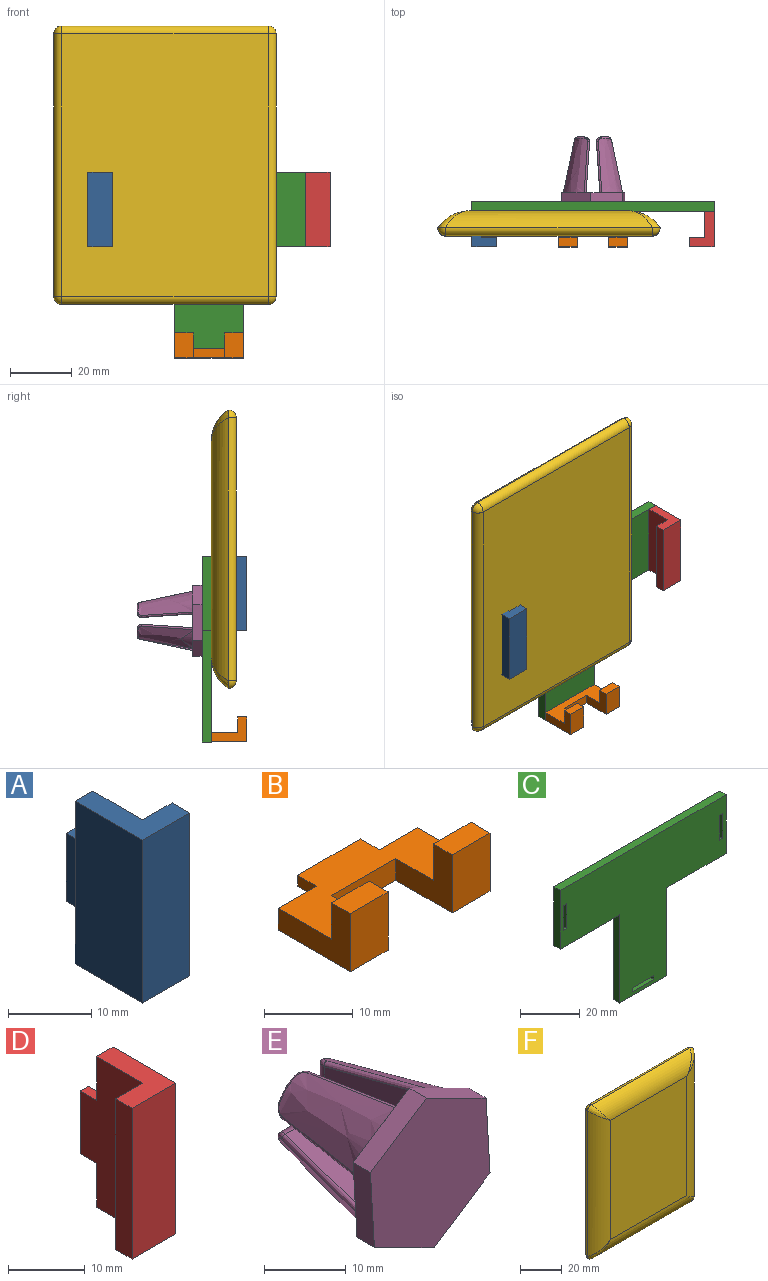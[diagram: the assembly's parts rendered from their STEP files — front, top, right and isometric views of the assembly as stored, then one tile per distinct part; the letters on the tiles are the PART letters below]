
ASSEMBLY  parts=6 mates=5
PART A: 12 faces, bbox 8x14.5x24 mm
  f0: plane 11.5x8mm, normal (0,0,-1), area 49.5mm2, adj f1,f4,f5,f6,f7,f11
  f1: plane 24x11.5mm, normal (1,0,0), area 234mm2, adj f0,f2,f3,f7,f8,f10,f11
  f2: plane 11.5x8mm, normal (0,0,1), area 49.5mm2, adj f1,f4,f5,f6,f7,f11
  f3: plane 10x1.5mm, normal (0,1,0), area 15mm2, adj f1,f8,f9,f10
  f4: plane 24x11.5mm, normal (-1,0,0), area 276mm2, adj f0,f2,f6,f11
  f5: plane 24x3mm, normal (1,0,0), area 72mm2, adj f0,f2,f6,f7
  f6: plane 24x8mm, normal (0,-1,0), area 192mm2, adj f0,f2,f4,f5
  f7: plane 24x5mm, normal (0,1,0), area 120mm2, adj f0,f1,f2,f5
  f8: plane 3x1.5mm, normal (0,0,1), area 4.5mm2, adj f1,f3,f9,f11
  f9: plane 10x3mm, normal (-1,0,0), area 30mm2, adj f3,f8,f10,f11
  f10: plane 3x1.5mm, normal (0,0,-1), area 4.5mm2, adj f1,f3,f9,f11
  f11: plane 24x3mm, normal (0,1,0), area 57mm2, adj f0,f1,f2,f4,f8,f9,f10
PART B: 18 faces, bbox 22.2x14.5x8 mm
  f0: plane 10x1.5mm, normal (0,1,0), area 15mm2, adj f1,f2,f3,f4
  f1: plane 22.2x11.5mm, normal (0,0,1), area 157.5mm2, adj f0,f3,f4,f5,f6,f7,f9,f12
  f2: plane 10x3mm, normal (0,0,-1), area 30mm2, adj f0,f3,f4,f5
  f3: plane 3x1.5mm, normal (-1,0,0), area 4.5mm2, adj f0,f1,f2,f5
  f4: plane 3x1.5mm, normal (1,0,0), area 4.5mm2, adj f0,f1,f2,f5
  f5: plane 22.2x3mm, normal (0,1,0), area 51.6mm2, adj f1,f2,f3,f4,f7,f8,f16
  f6: plane 9x8mm, normal (1,0,0), area 42mm2, adj f1,f8,f9,f10,f11,f17
  f7: plane 11.5x8mm, normal (-1,0,0), area 49.5mm2, adj f1,f5,f8,f9,f10,f11
  f8: plane 22.2x11.5mm, normal (0,0,-1), area 163.5mm2, adj f5,f6,f7,f11,f12,f15,f16,f17
  f9: plane 6x5mm, normal (0,1,0), area 30mm2, adj f1,f6,f7,f10
  f10: plane 6x3mm, normal (0,0,1), area 18mm2, adj f6,f7,f9,f11
  f11: plane 8x6mm, normal (0,-1,0), area 48mm2, adj f6,f7,f8,f10
  f12: plane 9x8mm, normal (-1,0,0), area 42mm2, adj f1,f8,f13,f14,f15,f17
  f13: plane 6x5mm, normal (0,1,0), area 30mm2, adj f1,f12,f14,f16
  f14: plane 6x3mm, normal (0,0,1), area 18mm2, adj f12,f13,f15,f16
  f15: plane 8x6mm, normal (0,-1,0), area 48mm2, adj f8,f12,f14,f16
  f16: plane 11.5x8mm, normal (1,0,0), area 49.5mm2, adj f1,f5,f8,f13,f14,f15
  f17: plane 10.2x3mm, normal (0,-1,0), area 30.6mm2, adj f1,f6,f8,f12
PART C: 22 faces, bbox 78.3x3x60 mm
  f0: plane 36x3mm, normal (-1,0,0), area 108mm2, adj f2,f3,f4,f5
  f1: plane 36x3mm, normal (1,0,0), area 108mm2, adj f2,f3,f4,f9
  f2: plane 22.2x3mm, normal (0,0,-1), area 66.6mm2, adj f0,f1,f3,f4
  f3: plane 78.3x60mm, normal (0,1,0), area 2629.9mm2, adj f0,f1,f2,f5,f6,f7,f8,f9
  f4: plane 78.3x60mm, normal (0,-1,0), area 2629.9mm2, adj f0,f1,f2,f5,f6,f7,f8,f9
  f5: plane 28.05x3mm, normal (0,0,-1), area 84.1mm2, adj f0,f3,f4,f8
  f6: plane 24x3mm, normal (1,0,0), area 72mm2, adj f3,f4,f7,f9
  f7: plane 78.3x3mm, normal (0,0,1), area 234.9mm2, adj f3,f4,f6,f8
  f8: plane 24x3mm, normal (-1,0,0), area 72mm2, adj f3,f4,f5,f7
  f9: plane 28.05x3mm, normal (0,0,-1), area 84.1mm2, adj f1,f3,f4,f6
  f10: plane 10.1x3mm, normal (1,0,0), area 30.3mm2, adj f3,f4,f11,f12
  f11: plane 3x1.6mm, normal (0,0,-1), area 4.8mm2, adj f3,f4,f10,f13
  f12: plane 3x1.6mm, normal (0,0,1), area 4.8mm2, adj f3,f4,f10,f13
  f13: plane 10.1x3mm, normal (-1,0,0), area 30.3mm2, adj f3,f4,f11,f12
  f14: plane 10.1x3mm, normal (0,0,1), area 30.3mm2, adj f3,f4,f15,f16
  f15: plane 3x1.6mm, normal (1,0,0), area 4.8mm2, adj f3,f4,f14,f17
  f16: plane 3x1.6mm, normal (-1,0,0), area 4.8mm2, adj f3,f4,f14,f17
  f17: plane 10.1x3mm, normal (0,0,-1), area 30.3mm2, adj f3,f4,f15,f16
  f18: plane 10.1x3mm, normal (1,0,0), area 30.3mm2, adj f3,f4,f19,f20
  f19: plane 3x1.6mm, normal (0,0,-1), area 4.8mm2, adj f3,f4,f18,f21
  f20: plane 3x1.6mm, normal (0,0,1), area 4.8mm2, adj f3,f4,f18,f21
  f21: plane 10.1x3mm, normal (-1,0,0), area 30.3mm2, adj f3,f4,f19,f20
PART D: 12 faces, bbox 8x14.5x24 mm
  f0: plane 11.5x8mm, normal (0,0,-1), area 49.5mm2, adj f1,f3,f5,f6,f7,f11
  f1: plane 24x11.5mm, normal (1,0,0), area 276mm2, adj f0,f4,f6,f11
  f2: plane 10x1.5mm, normal (0,1,0), area 15mm2, adj f3,f8,f9,f10
  f3: plane 24x11.5mm, normal (-1,0,0), area 234mm2, adj f0,f2,f4,f7,f8,f10,f11
  f4: plane 11.5x8mm, normal (0,0,1), area 49.5mm2, adj f1,f3,f5,f6,f7,f11
  f5: plane 24x3mm, normal (-1,0,0), area 72mm2, adj f0,f4,f6,f7
  f6: plane 24x8mm, normal (0,-1,0), area 192mm2, adj f0,f1,f4,f5
  f7: plane 24x5mm, normal (0,1,0), area 120mm2, adj f0,f3,f4,f5
  f8: plane 3x1.5mm, normal (0,0,-1), area 4.5mm2, adj f2,f3,f9,f11
  f9: plane 10x3mm, normal (1,0,0), area 30mm2, adj f2,f8,f10,f11
  f10: plane 3x1.5mm, normal (0,0,1), area 4.5mm2, adj f2,f3,f9,f11
  f11: plane 24x3mm, normal (0,1,0), area 57mm2, adj f0,f1,f3,f4,f8,f9,f10
PART E: 60 faces, bbox 40.8x31.4x31.2 mm
  f0: bspline ~17.61x8.12mm, area 143.4mm2, adj f4,f18,f19,f20,f48,f52
  f1: bspline ~17.61x8.12mm, area 143.4mm2, adj f4,f22,f23,f24,f43,f47
  f2: bspline ~17.61x8.12mm, area 143.4mm2, adj f4,f26,f27,f28,f38,f42
  f3: bspline ~17.61x8.12mm, area 143.4mm2, adj f4,f30,f31,f32,f33,f37
  f4: plane 40.77x31.17mm, normal (0,1,0), area 127.2mm2, adj f0,f1,f2,f3,f6,f7,f9,f10
  f5: plane 2.36x2.36mm, normal (0,1,0), area 3.3mm2, adj f31,f34,f36
  f6: plane 16.4x7.48mm, normal (-1,-0.07,0), area 85.4mm2, adj f4,f29,f32,f34
  f7: plane 16.4x7.48mm, normal (0,-0.07,-1), area 85.4mm2, adj f4,f29,f30,f36
  f8: plane 2.36x2.36mm, normal (0,1,0), area 3.3mm2, adj f27,f39,f41
  f9: plane 16.4x7.48mm, normal (1,-0.07,0), area 85.4mm2, adj f4,f25,f28,f39
  f10: plane 16.4x7.48mm, normal (0,-0.07,-1), area 85.4mm2, adj f4,f25,f26,f41
  f11: plane 2.36x2.36mm, normal (0,1,0), area 3.3mm2, adj f23,f44,f46
  f12: plane 16.4x7.48mm, normal (-1,-0.07,0), area 85.4mm2, adj f4,f21,f24,f44
  f13: plane 16.4x7.48mm, normal (0,-0.07,1), area 85.4mm2, adj f4,f21,f22,f46
  f14: plane 2.36x2.36mm, normal (0,1,0), area 3.3mm2, adj f19,f49,f51
  f15: plane 16.4x7.48mm, normal (0,-0.07,1), area 85.4mm2, adj f4,f17,f20,f49
  f16: plane 16.4x7.48mm, normal (1,-0.07,0), area 85.4mm2, adj f4,f17,f18,f51
  f17: cylinder r=0.5mm len=16.41mm, axis (-0.07,-1,-0.07), area 12.9mm2, adj f4,f15,f16,f50
  f18: bspline ~22.72x5.45mm, area 15.7mm2, adj f0,f4,f16,f52
  f19: bspline ~3.89x3.54mm, area 2.4mm2, adj f0,f14,f48,f52
  f20: bspline ~22.72x5.45mm, area 15.7mm2, adj f0,f4,f15,f48
  f21: cylinder r=0.5mm len=16.41mm, axis (0.07,-1,-0.07), area 12.9mm2, adj f4,f12,f13,f45
  f22: bspline ~22.72x5.45mm, area 15.7mm2, adj f1,f4,f13,f47
  f23: bspline ~3.89x3.54mm, area 2.4mm2, adj f1,f11,f43,f47
  f24: bspline ~22.72x5.45mm, area 15.7mm2, adj f1,f4,f12,f43
  f25: cylinder r=0.5mm len=16.41mm, axis (-0.07,-1,0.07), area 12.9mm2, adj f4,f9,f10,f40
  f26: bspline ~22.72x5.45mm, area 15.7mm2, adj f2,f4,f10,f42
  f27: bspline ~3.89x3.54mm, area 2.4mm2, adj f2,f8,f38,f42
  f28: bspline ~22.72x5.45mm, area 15.7mm2, adj f2,f4,f9,f38
  f29: cylinder r=0.5mm len=16.41mm, axis (-0.07,1,-0.07), area 12.9mm2, adj f4,f6,f7,f35
  f30: bspline ~20.18x4.91mm, area 15.7mm2, adj f3,f4,f7,f37
  f31: bspline ~3.62x3.43mm, area 2.4mm2, adj f3,f5,f33,f37
  f32: bspline ~20.18x4.91mm, area 15.7mm2, adj f3,f4,f6,f33
  f33: bspline ~2.03x1.75mm, area 1.9mm2, adj f3,f31,f32,f34
  f34: cylinder r=1.5mm len=4mm, axis (0,0,-1), area 7.8mm2, adj f5,f6,f33,f35
  f35: bspline ~1.76x1.5mm, area 0.9mm2, adj f29,f34,f36
  f36: cylinder r=1.5mm len=4mm, axis (-1,0,0), area 7.8mm2, adj f5,f7,f35,f37
  f37: bspline ~1.99x1.93mm, area 1.9mm2, adj f3,f30,f31,f36
  f38: bspline ~1.99x1.93mm, area 1.9mm2, adj f2,f27,f28,f39
  f39: cylinder r=1.5mm len=4mm, axis (0,0,-1), area 7.8mm2, adj f8,f9,f38,f40
  f40: bspline ~1.76x1.5mm, area 0.9mm2, adj f25,f39,f41
  f41: cylinder r=1.5mm len=4mm, axis (1,0,0), area 7.8mm2, adj f8,f10,f40,f42
  f42: bspline ~2.03x1.75mm, area 1.9mm2, adj f2,f26,f27,f41
  f43: bspline ~1.99x1.93mm, area 1.9mm2, adj f1,f23,f24,f44
  f44: cylinder r=1.5mm len=4mm, axis (0,0,1), area 7.8mm2, adj f11,f12,f43,f45
  f45: bspline ~1.76x1.5mm, area 0.9mm2, adj f21,f44,f46
  f46: cylinder r=1.5mm len=4mm, axis (-1,0,0), area 7.8mm2, adj f11,f13,f45,f47
  f47: bspline ~2.03x1.75mm, area 1.9mm2, adj f1,f22,f23,f46
  f48: bspline ~1.99x1.93mm, area 1.9mm2, adj f0,f19,f20,f49
  f49: cylinder r=1.5mm len=4mm, axis (1,0,0), area 7.8mm2, adj f14,f15,f48,f50
  f50: bspline ~1.76x1.5mm, area 0.9mm2, adj f17,f49,f51
  f51: cylinder r=1.5mm len=4mm, axis (0,0,1), area 7.8mm2, adj f14,f16,f50,f52
  f52: bspline ~2.03x1.75mm, area 1.9mm2, adj f0,f18,f19,f51
  f53: plane 11.53x3mm, normal (-1,0,-0.06), area 34.6mm2, adj f4,f54,f58,f59
  f54: plane 9.64x6.35mm, normal (-0.55,0,0.84), area 34.6mm2, adj f4,f53,f55,f59
  f55: plane 10.32x5.18mm, normal (0.45,0,0.89), area 34.6mm2, adj f4,f54,f56,f59
  f56: plane 11.53x3mm, normal (1,0,0.06), area 34.6mm2, adj f4,f55,f57,f59
  f57: plane 9.64x6.35mm, normal (0.55,0,-0.84), area 34.6mm2, adj f4,f56,f58,f59
  f58: plane 23.01x11.54mm, normal (-0.45,0,-0.89), area 34.6mm2, adj f4,f53,f57,f59
  f59: plane 23.05x20.65mm, normal (0,-1,0), area 346.4mm2, adj f53,f54,f55,f56,f57,f58
PART F: 18 faces, bbox 71.8x8x90 mm
  f0: plane 69.83x51.63mm, normal (0,-1,0), area 3604.8mm2, adj f10,f13,f14,f17
  f1: plane 85x66.8mm, normal (0,1,0), area 5678mm2, adj f3,f4,f7,f8
  f2: sphere r=2.5mm, area 9.8mm2, adj f3,f4,f11
  f3: cylinder r=2.5mm len=66.8mm, axis (-1,0,0), area 262.3mm2, adj f1,f2,f5,f13
  f4: cylinder r=2.5mm len=85mm, axis (0,0,-1), area 333.8mm2, adj f1,f2,f6,f10
  f5: sphere r=2.5mm, area 13.4mm2, adj f3,f7,f15
  f6: sphere r=2.5mm, area 9.8mm2, adj f4,f8,f12
  f7: cylinder r=2.5mm len=85mm, axis (0,0,1), area 333.8mm2, adj f1,f5,f9,f17
  f8: cylinder r=2.5mm len=66.8mm, axis (1,0,0), area 262.3mm2, adj f1,f6,f9,f14
  f9: sphere r=2.5mm, area 6.2mm2, adj f7,f8,f16
  f10: cylinder r=12mm len=85mm, axis (0,0,-1), area 927.4mm2, adj f0,f4,f11,f12
  f11: bspline ~10.09x10.09mm, area 19mm2, adj f2,f10,f13
  f12: bspline ~10.09x10.09mm, area 19mm2, adj f6,f10,f14
  f13: cylinder r=12mm len=66.8mm, axis (1,0,0), area 709.4mm2, adj f0,f3,f11,f15
  f14: cylinder r=12mm len=66.8mm, axis (1,0,0), area 709.4mm2, adj f0,f8,f12,f16
  f15: bspline ~10.09x10.09mm, area 19.1mm2, adj f5,f13,f17
  f16: bspline ~10.09x10.09mm, area 19.1mm2, adj f9,f14,f17
  f17: cylinder r=12mm len=85mm, axis (0,0,-1), area 927.4mm2, adj f0,f7,f15,f16
PLACE A t=(-65.62,-27.32,27.97)mm
PLACE B t=(-78.62,-27.32,41.07)mm
PLACE C t=(-78.62,-27.32,27.97)mm
PLACE D t=(-91.62,-27.32,27.97)mm
PLACE E t=(-78.62,-44.32,19.13)mm
PLACE F rot(axis=(1,0,0),180deg) t=(-231.56,-55.32,-20.56)mm
MATE fastened B.f0 <-> C.f3  axis (0,1,0) through (-78.62,-44.32,-16.93)mm
MATE fastened E.f59 <-> C.f3  axis (0,-1,0) through (-78.62,-44.32,19.13)mm
MATE planar C.f4 <-> F.f0  axis (0,-1,0) through (-78.62,-47.32,19.13)mm
MATE fastened D.f2 <-> C.f3  axis (0,1,0) through (-40.97,-44.32,27.97)mm
MATE fastened A.f3 <-> C.f3  axis (0,1,0) through (-116.27,-44.32,27.97)mm
